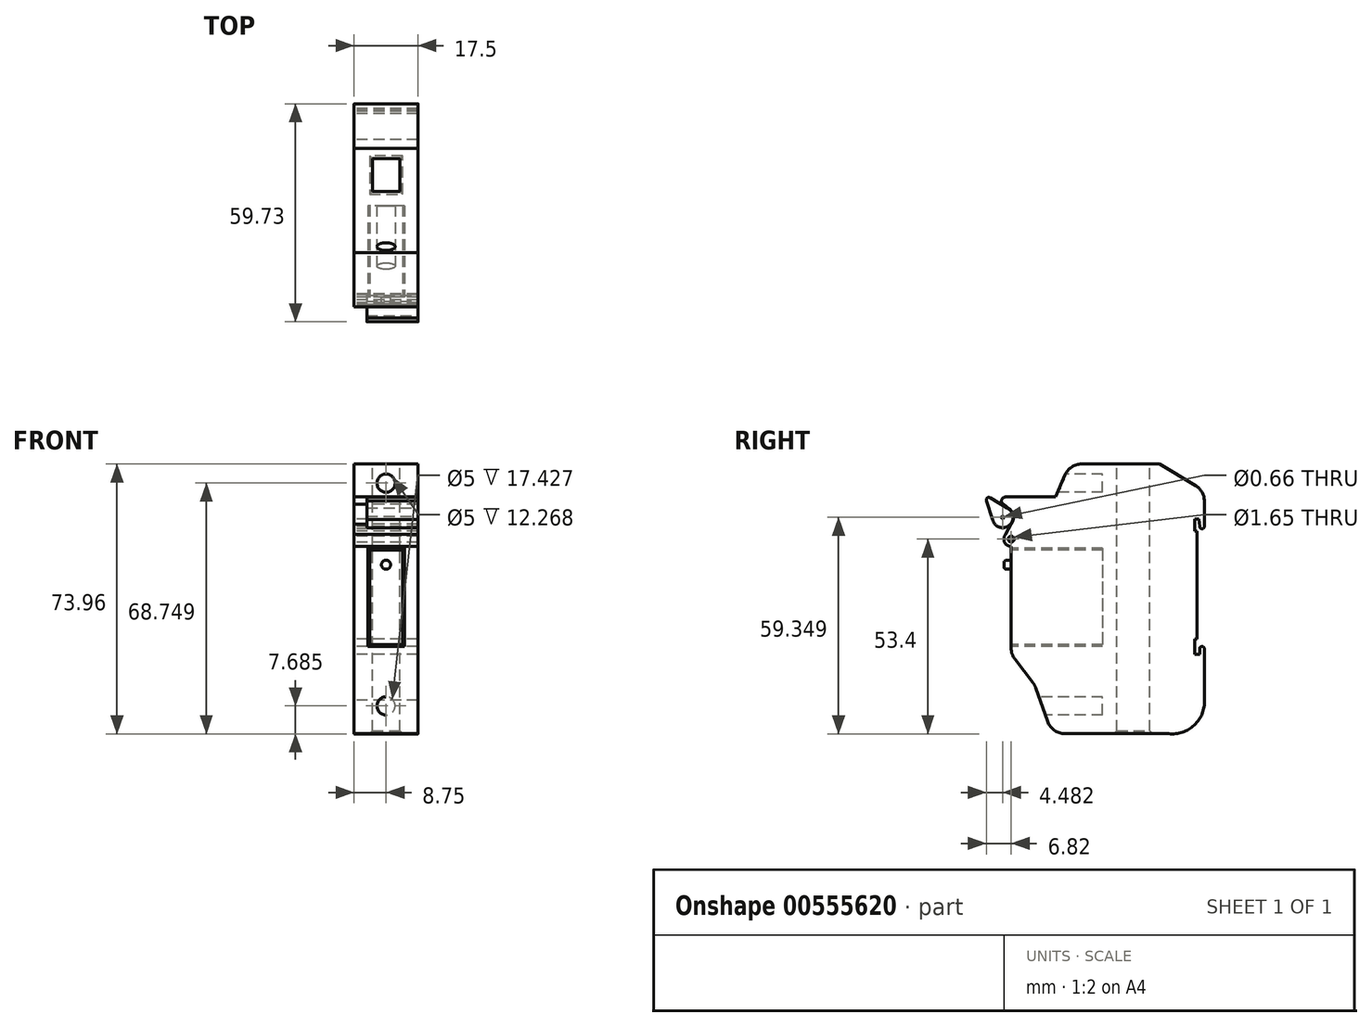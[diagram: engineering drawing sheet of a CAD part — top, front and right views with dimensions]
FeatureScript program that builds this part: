
annotation { "Feature Type Name" : "Feature", "Feature Type Description" : "" }
export const myFeature = defineFeature(function(context is Context, id is Id, definition is map)
    precondition{}
    {
        {
            var Q0;
            Q0=qCreatedBy(makeId("Right.planeOp"),FACE);
            var sketch = newSketch(context, id + "F0", { "sketchPlane" : qUnion([Q0])});
            skLineSegment(sketch, "E0", {"start": v(0, 86.45) * mm, "end": v(0, 33.6) * mm, "construction": true});
            skLineSegment(sketch, "E1", {"start": v(-101.47, 0) * mm, "end": v(113.77, 0) * mm, "construction": true});
            skLineSegment(sketch, "E2", {"start": v(0, 0) * mm, "end": v(0, -40.3) * mm});
            skLineSegment(sketch, "E3", {"start": v(14.7, -40.3) * mm, "end": v(45.1, -40.3) * mm});
            skLineSegment(sketch, "E4", {"start": v(52.9, -32.04) * mm, "end": v(52.9, -17.04) * mm});
            skLineSegment(sketch, "E5", {"start": v(40.66, 33.6) * mm, "end": v(19.3, 33.6) * mm});
            skLineSegment(sketch, "E6.bottom", {"start": v(51.37, 18.6) * mm, "end": v(50.3, 18.6) * mm});
            skLineSegment(sketch, "E6.top", {"start": v(52.9, -18.6) * mm, "end": v(50.3, -18.6) * mm});
            skLineSegment(sketch, "E6.right", {"start": v(50.3, 18.6) * mm, "end": v(50.3, 15.23) * mm});
            skPoint(sketch, "E6.middle", {"position": v(52.9, 0) * mm});
            skLineSegment(sketch, "E7", {"start": v(51.37, 18.6) * mm, "end": v(51.6, 16.51) * mm});
            skLineSegment(sketch, "E8.bottom", {"start": v(50.3, 15.23) * mm, "end": v(50.92, 15.23) * mm});
            skLineSegment(sketch, "E8.top", {"start": v(50.3, -14.35) * mm, "end": v(50.92, -14.35) * mm});
            skLineSegment(sketch, "E8.right", {"start": v(50.92, 15.23) * mm, "end": v(50.92, -14.35) * mm});
            skPoint(sketch, "E9.orphan", {"position": v(55.5, -18.6) * mm});
            skPoint(sketch, "E6.left.start.orphan", {"position": v(55.5, 18.6) * mm});
            skLineSegment(sketch, "E10.trimOffspring", {"start": v(52.9, 16.51) * mm, "end": v(52.9, 23.43) * mm});
            skLineSegment(sketch, "E11", {"start": v(51.6, -18.6) * mm, "end": v(51.6, -17.04) * mm});
            skLineSegment(sketch, "E12", {"start": v(52.9, -17.04) * mm, "end": v(52.9, -18.6) * mm});
            skArc(sketch, "E13", {"start": v(52.9, -17.04) * mm, "mid": v(52.25, -16.4) * mm, "end": v(51.6, -17.04) * mm});
            skArc(sketch, "E14", {"start": v(51.6, 16.51) * mm, "mid": v(52.25, 15.86) * mm, "end": v(52.9, 16.51) * mm});
            skLineSegment(sketch, "E15.trimOffspring", {"start": v(50.3, -14.35) * mm, "end": v(50.3, -18.6) * mm});
            skLineSegment(sketch, "E16", {"start": v(50.47, 27.72) * mm, "end": v(40.66, 33.6) * mm});
            skArc(sketch, "E17", {"start": v(43.12, -40.3) * mm, "mid": v(50.15, -37.96) * mm, "end": v(52.9, -31.07) * mm});
            skLineSegment(sketch, "E18.trimOffspring", {"start": v(0, -40.3) * mm, "end": v(0, -83.55) * mm, "construction": true});
            skLineSegment(sketch, "E19", {"start": v(9.98, -36.97) * mm, "end": v(6.69, -27.67) * mm});
            skLineSegment(sketch, "E20", {"start": v(5.93, -26.28) * mm, "end": v(1.04, -19.95) * mm});
            skLineSegment(sketch, "E21", {"start": v(0, 24.58) * mm, "end": v(12.18, 24.58) * mm});
            skLineSegment(sketch, "E22", {"start": v(12.18, 24.58) * mm, "end": v(14.7, 30.55) * mm});
            skArc(sketch, "E23", {"start": v(0, 17.15) * mm, "mid": v(0.61, 19.37) * mm, "end": v(-0.55, 21.36) * mm});
            skCircle(sketch, "E24", {"center": v(0, 13.04) * mm, "radius": 0.82 * mm});
            skArc(sketch, "E25", {"start": v(-1.54, 14.34) * mm, "mid": v(-1.83, 12.2) * mm, "end": v(0, 11.03) * mm});
            skLineSegment(sketch, "E26", {"start": v(-1.54, 14.34) * mm, "end": v(0.26, 17.53) * mm});
            skArc(sketch, "E27", {"start": v(-1.57, 24.58) * mm, "mid": v(-2.62, 23.78) * mm, "end": v(-2.13, 22.56) * mm});
            skLineSegment(sketch, "E28", {"start": v(0, 24.58) * mm, "end": v(-1.57, 24.58) * mm});
            skLineSegment(sketch, "E29", {"start": v(-2.13, 22.56) * mm, "end": v(-0.55, 21.36) * mm});
            skLineSegment(sketch, "E30.trimOffspring", {"start": v(0, 11.03) * mm, "end": v(0, -16.9) * mm, "construction": true});
            skLineSegment(sketch, "E31.trimOffspring", {"start": v(0, 11.03) * mm, "end": v(0, 0) * mm});
            skLineSegment(sketch, "E32.trimOffspring", {"start": v(0, 17.15) * mm, "end": v(0, 17.08) * mm, "construction": true});
            skLineSegment(sketch, "E33.trimOffspring", {"start": v(0, 17.15) * mm, "end": v(0, 17.08) * mm});
            skPoint(sketch, "E34.visualSharp", {"position": v(0, -18.6) * mm});
            skArc(sketch, "E34.filletArc", {"start": v(0, -16.9) * mm, "mid": v(0.27, -18.5) * mm, "end": v(1.04, -19.95) * mm});
            skPoint(sketch, "E35.visualSharp", {"position": v(6.42, -26.91) * mm});
            skArc(sketch, "E35.filletArc", {"start": v(6.69, -27.67) * mm, "mid": v(6.36, -26.94) * mm, "end": v(5.93, -26.28) * mm});
            skPoint(sketch, "E36.visualSharp", {"position": v(11.16, -40.3) * mm});
            skArc(sketch, "E36.filletArc", {"start": v(9.98, -36.97) * mm, "mid": v(11.8, -39.38) * mm, "end": v(14.7, -40.3) * mm});
            skPoint(sketch, "E37.visualSharp", {"position": v(15.99, 33.6) * mm});
            skArc(sketch, "E37.filletArc", {"start": v(19.3, 33.6) * mm, "mid": v(16.54, 32.77) * mm, "end": v(14.7, 30.55) * mm});
            skPoint(sketch, "E38.visualSharp", {"position": v(52.9, 26.27) * mm});
            skArc(sketch, "E38.filletArc", {"start": v(52.9, 23.43) * mm, "mid": v(52.25, 25.9) * mm, "end": v(50.47, 27.72) * mm});
            skSolve(sketch);
        }
        {
            var Q0;
            Q0 = qSketchRegion(id + "F0", true);
            extrude(context, id + "F1", {"entities" : qUnion([Q0]), "depth" : 17.5 * mm, "offsetDistance" : 25 * mm});
        }
        {
            var Q0;
            Q0=makeQuery(id+"F1.opExtrude","CAP_FACE",FACE,{"disambiguationData":[OSD([sQuery(id+"F0.wireOp",EDGE,"E2"),sQuery(id+"F0.wireOp",EDGE,"E3"),sQuery(id+"F0.wireOp",EDGE,"E4"),sQuery(id+"F0.wireOp",EDGE,"E5"),sQuery(id+"F0.wireOp",EDGE,"E6.bottom"),sQuery(id+"F0.wireOp",EDGE,"E6.top"),sQuery(id+"F0.wireOp",EDGE,"E6.right"),sQuery(id+"F0.wireOp",EDGE,"E7"),sQuery(id+"F0.wireOp",EDGE,"E8.bottom"),sQuery(id+"F0.wireOp",EDGE,"E8.top"),sQuery(id+"F0.wireOp",EDGE,"E8.right"),sQuery(id+"F0.wireOp",EDGE,"E10.trimOffspring"),sQuery(id+"F0.wireOp",EDGE,"E11"),sQuery(id+"F0.wireOp",EDGE,"E12"),sQuery(id+"F0.wireOp",EDGE,"E13"),sQuery(id+"F0.wireOp",EDGE,"E14"),sQuery(id+"F0.wireOp",EDGE,"E15.trimOffspring"),sQuery(id+"F0.wireOp",EDGE,"E16"),sQuery(id+"F0.wireOp",EDGE,"E17"),sQuery(id+"F0.wireOp",EDGE,"E19"),sQuery(id+"F0.wireOp",EDGE,"E20"),sQuery(id+"F0.wireOp",EDGE,"E21"),sQuery(id+"F0.wireOp",EDGE,"E22"),sQuery(id+"F0.wireOp",EDGE,"E23"),sQuery(id+"F0.wireOp",EDGE,"E24"),sQuery(id+"F0.wireOp",EDGE,"E25"),sQuery(id+"F0.wireOp",EDGE,"E26"),sQuery(id+"F0.wireOp",EDGE,"E27"),sQuery(id+"F0.wireOp",EDGE,"E28"),sQuery(id+"F0.wireOp",EDGE,"E29"),sQuery(id+"F0.wireOp",EDGE,"E31.trimOffspring"),sQuery(id+"F0.wireOp",EDGE,"E33.trimOffspring"),sQuery(id+"F0.wireOp",EDGE,"E34.filletArc"),sQuery(id+"F0.wireOp",EDGE,"E35.filletArc"),sQuery(id+"F0.wireOp",EDGE,"E36.filletArc"),sQuery(id+"F0.wireOp",EDGE,"E37.filletArc"),sQuery(id+"F0.wireOp",EDGE,"E38.filletArc")])],"isStart":false});
            var sketch = newSketch(context, id + "F2", { "sketchPlane" : qUnion([Q0])});
            skArc(sketch, "E39", {"start": v(-5.1, 18.4) * mm, "mid": v(-0.56, 16.8) * mm, "end": v(-1.2, 21.57) * mm});
            skArc(sketch, "E40", {"start": v(-5.77, 24.34) * mm, "mid": v(-6.6, 24.31) * mm, "end": v(-6.73, 23.5) * mm});
            skLineSegment(sketch, "E41", {"start": v(-6.73, 23.5) * mm, "end": v(-4.92, 17.86) * mm});
            skLineSegment(sketch, "E42", {"start": v(-5.77, 24.34) * mm, "end": v(-1.2, 21.57) * mm});
            skCircle(sketch, "E43", {"center": v(-2.34, 18.99) * mm, "radius": 0.33 * mm});
            skSolve(sketch);
        }
        {
            var Q0;
            Q0 = qSketchRegion(id + "F2", true);
            extrude(context, id + "F3", {"entities" : qUnion([Q0]), "oppositeDirection" : true, "depth" : 14 * mm, "offsetDistance" : 25 * mm});
        }
        {
            var Q0;
            Q0=makeQuery(id+"F1.opExtrude","SWEPT_FACE",FACE,{"disambiguationData":[OSD([sQuery(id+"F0.wireOp",EDGE,"E5")])]});
            var sketch = newSketch(context, id + "F4", { "sketchPlane" : qUnion([Q0])});
            skLineSegment(sketch, "E44.bottom", {"start": v(5, 37.9) * mm, "end": v(12.5, 37.9) * mm});
            skLineSegment(sketch, "E44.top", {"start": v(5, 28.9) * mm, "end": v(12.5, 28.9) * mm});
            skLineSegment(sketch, "E44.left", {"start": v(5, 37.9) * mm, "end": v(5, 28.9) * mm});
            skLineSegment(sketch, "E44.right", {"start": v(12.5, 37.9) * mm, "end": v(12.5, 28.9) * mm});
            skPoint(sketch, "E44.middle", {"position": v(8.75, 33.4) * mm});
            skPoint(sketch, "E44.middle.positionSnap0", {"position": v(8.75, 19.3) * mm});
            skPoint(sketch, "E44.centerSnap0", {"position": v(8.75, 19.3) * mm});
            skSolve(sketch);
        }
        {
            var Q0;
            Q0 = qSketchRegion(id + "F4", true);
            extrude(context, id + "F5", {"entities" : qUnion([Q0]), "operationType" : NewBodyOperationType.REMOVE, "endBound" : BoundingType.THROUGH_ALL, "oppositeDirection" : true, "depth" : 25 * mm, "offsetDistance" : 25 * mm});
        }
        {
            var Q0;
            Q0=qCreatedBy(makeId("Front.planeOp"),FACE);
            var sketch = newSketch(context, id + "F6", { "sketchPlane" : qUnion([Q0])});
            skLineSegment(sketch, "E45", {"start": v(8.75, -59.1) * mm, "end": v(8.75, 50.81) * mm, "construction": true});
            skCircle(sketch, "E46", {"center": v(8.75, -32.68) * mm, "radius": 2.5 * mm});
            skCircle(sketch, "E47", {"center": v(8.75, 28.39) * mm, "radius": 2.5 * mm});
            skSolve(sketch);
        }
        {
            var Q0;
            Q0 = qSketchRegion(id + "F6", true);
            extrude(context, id + "F7", {"entities" : qUnion([Q0]), "operationType" : NewBodyOperationType.REMOVE, "oppositeDirection" : true, "depth" : 25 * mm, "offsetDistance" : 25 * mm});
        }
        {
            var Q0;
            Q0=makeQuery(id+"F1.opExtrude","SWEPT_FACE",FACE,{"disambiguationData":[OSD([sQuery(id+"F0.wireOp",EDGE,"E2"),sQuery(id+"F0.wireOp",EDGE,"E31.trimOffspring")])]});
            var sketch = newSketch(context, id + "F8", { "sketchPlane" : qUnion([Q0])});
            skLineSegment(sketch, "E48.bottom", {"start": v(13.75, 10.57) * mm, "end": v(3.75, 10.57) * mm});
            skLineSegment(sketch, "E48.top", {"start": v(13.75, -16.43) * mm, "end": v(3.75, -16.43) * mm});
            skLineSegment(sketch, "E48.left", {"start": v(13.75, 10.57) * mm, "end": v(13.75, -16.43) * mm});
            skLineSegment(sketch, "E48.right", {"start": v(3.75, 10.57) * mm, "end": v(3.75, -16.43) * mm});
            skPoint(sketch, "E48.middle", {"position": v(8.75, -2.93) * mm});
            skPoint(sketch, "E48.middle.positionSnap0", {"position": v(17.5, -2.93) * mm});
            skPoint(sketch, "E48.middle.positionSnap1", {"position": v(8.75, -16.9) * mm});
            skPoint(sketch, "E48.centerSnap0", {"position": v(17.5, -2.93) * mm});
            skPoint(sketch, "E48.centerSnap1", {"position": v(8.75, -16.9) * mm});
            skLineSegment(sketch, "E49.bottom", {"start": v(13.25, 10.07) * mm, "end": v(4.25, 10.07) * mm});
            skLineSegment(sketch, "E49.top", {"start": v(13.25, -15.93) * mm, "end": v(4.25, -15.93) * mm});
            skLineSegment(sketch, "E49.left", {"start": v(13.25, 10.07) * mm, "end": v(13.25, -15.93) * mm});
            skLineSegment(sketch, "E49.right", {"start": v(4.25, 10.07) * mm, "end": v(4.25, -15.93) * mm});
            skSolve(sketch);
        }
        {
            var Q0;
            Q0 = qSketchRegion(id + "F8", true);
            extrude(context, id + "F9", {"entities" : qUnion([Q0]), "operationType" : NewBodyOperationType.REMOVE, "oppositeDirection" : true, "depth" : 25 * mm, "offsetDistance" : 25 * mm});
        }
        {
            var Q0;
            Q0=makeQuery(id+"F9.boolean.opBoolean","SPLIT",FACE,{"disambiguationData":[TD([makeQuery(id+"F9.opExtrude","SWEPT_FACE",FACE,{"disambiguationData":[OSD([sQuery(id+"F8.wireOp",EDGE,"E49.bottom")])]})])],"derivedFrom":makeQuery(id+"F1.opExtrude","SWEPT_FACE",FACE,{"disambiguationData":[OSD([sQuery(id+"F0.wireOp",EDGE,"E2"),sQuery(id+"F0.wireOp",EDGE,"E31.trimOffspring")])]})});
            var sketch = newSketch(context, id + "F10", { "sketchPlane" : qUnion([Q0])});
            skCircle(sketch, "E50", {"center": v(8.75, 6.02) * mm, "radius": 1.25 * mm});
            skPoint(sketch, "E50.centerSnap0", {"position": v(8.75, 10.07) * mm});
            skSolve(sketch);
        }
        {
            var Q0;
            Q0 = qSketchRegion(id + "F10", true);
            extrude(context, id + "F11", {"entities" : qUnion([Q0]), "operationType" : NewBodyOperationType.ADD, "depth" : 2 * mm, "offsetDistance" : 25 * mm});
        }
        {
            var Q0;
            Q0=makeQuery(id+"F11.opExtrude","CAP_EDGE",EDGE,{"disambiguationData":[OSD([sQuery(id+"F10.wireOp",EDGE,"E50")])],"isStart":false});
            fillet(context, id + "F12", {"entities" : qUnion([Q0]), "radius" : .75 * mm, "tangentPropagation" : true, "allowEdgeOverflow" : false});
        }
        {
            var Q0;
            Q0=makeQuery(id+"F5.boolean.opBoolean","INTERSECT",EDGE,{"derivedFrom":[makeQuery(id+"F1.opExtrude","SWEPT_FACE",FACE,{"disambiguationData":[OSD([sQuery(id+"F0.wireOp",EDGE,"E3")])]}),makeQuery(id+"F5.opExtrude","SWEPT_FACE",FACE,{"disambiguationData":[OSD([sQuery(id+"F4.wireOp",EDGE,"E44.bottom")])]})]});
            var Q1;
            Q1=makeQuery(id+"F5.boolean.opBoolean","INTERSECT",EDGE,{"derivedFrom":[makeQuery(id+"F1.opExtrude","SWEPT_FACE",FACE,{"disambiguationData":[OSD([sQuery(id+"F0.wireOp",EDGE,"E3")])]}),makeQuery(id+"F5.opExtrude","SWEPT_FACE",FACE,{"disambiguationData":[OSD([sQuery(id+"F4.wireOp",EDGE,"E44.right")])]})]});
            var Q2;
            Q2=makeQuery(id+"F5.boolean.opBoolean","INTERSECT",EDGE,{"derivedFrom":[makeQuery(id+"F1.opExtrude","SWEPT_FACE",FACE,{"disambiguationData":[OSD([sQuery(id+"F0.wireOp",EDGE,"E3")])]}),makeQuery(id+"F5.opExtrude","SWEPT_FACE",FACE,{"disambiguationData":[OSD([sQuery(id+"F4.wireOp",EDGE,"E44.top")])]})]});
            var Q3;
            Q3=makeQuery(id+"F5.boolean.opBoolean","INTERSECT",EDGE,{"derivedFrom":[makeQuery(id+"F1.opExtrude","SWEPT_FACE",FACE,{"disambiguationData":[OSD([sQuery(id+"F0.wireOp",EDGE,"E3")])]}),makeQuery(id+"F5.opExtrude","SWEPT_FACE",FACE,{"disambiguationData":[OSD([sQuery(id+"F4.wireOp",EDGE,"E44.left")])]})]});
            var Q4;
            Q4=makeQuery(id+"F5.boolean.opBoolean","COPY",EDGE,{"derivedFrom":makeQuery(id+"F5.opExtrude","CAP_EDGE",EDGE,{"disambiguationData":[OSD([sQuery(id+"F4.wireOp",EDGE,"E44.left")])],"isStart":true})});
            var Q5;
            Q5=makeQuery(id+"F5.boolean.opBoolean","COPY",EDGE,{"derivedFrom":makeQuery(id+"F5.opExtrude","CAP_EDGE",EDGE,{"disambiguationData":[OSD([sQuery(id+"F4.wireOp",EDGE,"E44.top")])],"isStart":true})});
            var Q6;
            Q6=makeQuery(id+"F5.boolean.opBoolean","COPY",EDGE,{"derivedFrom":makeQuery(id+"F5.opExtrude","CAP_EDGE",EDGE,{"disambiguationData":[OSD([sQuery(id+"F4.wireOp",EDGE,"E44.right")])],"isStart":true})});
            var Q7;
            Q7=makeQuery(id+"F5.boolean.opBoolean","COPY",EDGE,{"derivedFrom":makeQuery(id+"F5.opExtrude","CAP_EDGE",EDGE,{"disambiguationData":[OSD([sQuery(id+"F4.wireOp",EDGE,"E44.bottom")])],"isStart":true})});
            chamfer(context, id + "F13", {"entities" : qUnion([Q0, Q1, Q2, Q3, Q4, Q5, Q6, Q7]), "width" : .75 * mm, "tangentPropagation" : true});
        }
    });
